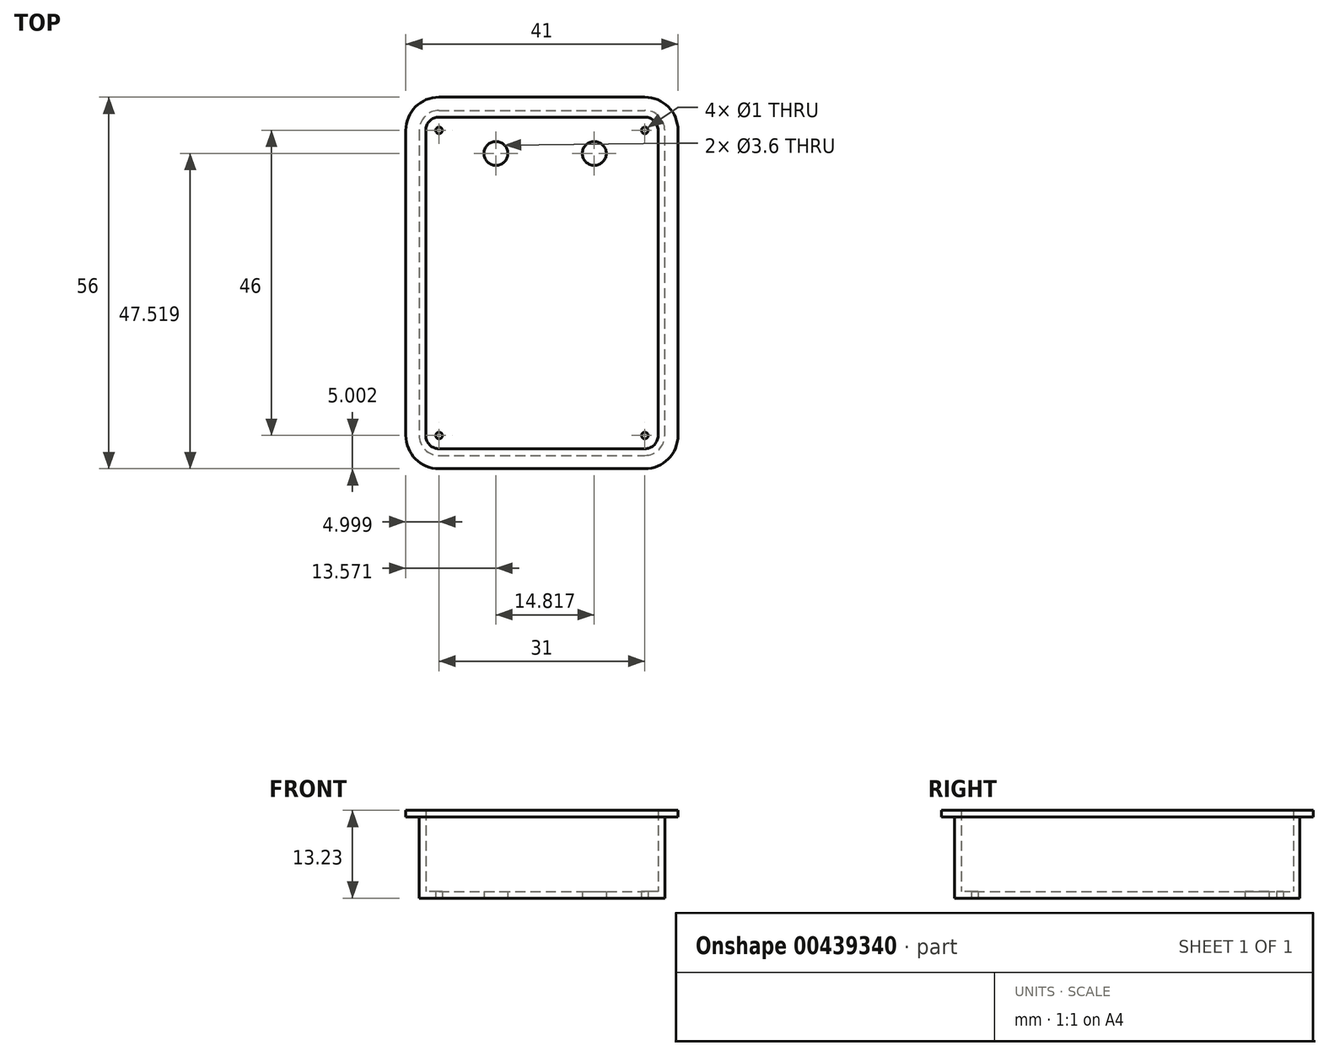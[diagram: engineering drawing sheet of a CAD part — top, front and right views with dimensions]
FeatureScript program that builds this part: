
annotation { "Feature Type Name" : "Feature", "Feature Type Description" : "" }
export const myFeature = defineFeature(function(context is Context, id is Id, definition is map)
    precondition{}
    {
        {
            var Q0;
            Q0=qCreatedBy(makeId("Top.planeOp"),FACE);
            var sketch = newSketch(context, id + "F0", { "sketchPlane" : qUnion([Q0])});
            skLineSegment(sketch, "E0.bottom", {"start": v(-15.84, -22.1) * mm, "end": v(15.16, -22.1) * mm});
            skLineSegment(sketch, "E0.top", {"start": v(-15.84, 27.9) * mm, "end": v(15.16, 27.9) * mm});
            skLineSegment(sketch, "E0.right", {"start": v(17.16, -20.1) * mm, "end": v(17.16, 25.9) * mm});
            skPoint(sketch, "E1.visualSharp", {"position": v(17.16, 27.9) * mm});
            skArc(sketch, "E1.filletArc", {"start": v(17.16, 25.9) * mm, "mid": v(16.57, 27.3) * mm, "end": v(15.16, 27.9) * mm});
            skPoint(sketch, "E2.visualSharp", {"position": v(17.16, -22.1) * mm});
            skArc(sketch, "E2.filletArc", {"start": v(15.16, -22.1) * mm, "mid": v(16.57, -21.52) * mm, "end": v(17.16, -20.1) * mm});
            skLineSegment(sketch, "E3", {"start": v(-17.84, 25.9) * mm, "end": v(-17.84, -20.1) * mm});
            skPoint(sketch, "E4.visualSharp", {"position": v(-17.84, 27.9) * mm});
            skArc(sketch, "E4.filletArc", {"start": v(-15.84, 27.9) * mm, "mid": v(-17.26, 27.3) * mm, "end": v(-17.84, 25.9) * mm});
            skPoint(sketch, "E5.visualSharp", {"position": v(-17.84, -22.1) * mm});
            skArc(sketch, "E5.filletArc", {"start": v(-17.84, -20.1) * mm, "mid": v(-17.26, -21.52) * mm, "end": v(-15.84, -22.1) * mm});
            skCircle(sketch, "E6", {"center": v(-15.84, -20.1) * mm, "radius": 0.5 * mm});
            skCircle(sketch, "E7", {"center": v(-15.84, 25.9) * mm, "radius": 0.5 * mm});
            skCircle(sketch, "E8", {"center": v(15.16, 25.9) * mm, "radius": 0.5 * mm});
            skCircle(sketch, "E9", {"center": v(15.16, -20.1) * mm, "radius": 0.5 * mm});
            skArc(sketch, "E10.0", {"start": v(-15.84, 28.9) * mm, "mid": v(-17.96, 28.01) * mm, "end": v(-18.84, 25.9) * mm});
            skLineSegment(sketch, "E10.1", {"start": v(-18.84, 25.9) * mm, "end": v(-18.84, -20.1) * mm});
            skLineSegment(sketch, "E10.2", {"start": v(-15.84, 28.9) * mm, "end": v(15.16, 28.9) * mm});
            skArc(sketch, "E10.3", {"start": v(-18.84, -20.1) * mm, "mid": v(-17.96, -22.23) * mm, "end": v(-15.84, -23.1) * mm});
            skArc(sketch, "E10.4", {"start": v(18.16, 25.9) * mm, "mid": v(17.28, 28.01) * mm, "end": v(15.16, 28.9) * mm});
            skLineSegment(sketch, "E10.5", {"start": v(18.16, -20.1) * mm, "end": v(18.16, 25.9) * mm});
            skArc(sketch, "E10.6", {"start": v(15.16, -23.1) * mm, "mid": v(17.28, -22.23) * mm, "end": v(18.16, -20.1) * mm});
            skLineSegment(sketch, "E10.7", {"start": v(-15.84, -23.1) * mm, "end": v(15.16, -23.1) * mm});
            skSolve(sketch);
        }
        {
            var Q0;
            Q0=makeQuery(id+"F0.imprint","IMPRINT",FACE,{"disambiguationData":[TD([[makeQuery(id+"F0.imprint","IMPRINT",EDGE,{"derivedFrom":sQuery(id+"F0.wireOp",EDGE,"E0.bottom")}),1.0]])]});
            extrude(context, id + "F1", {"entities" : qUnion([Q0]), "depth" : 1 * mm});
        }
        {
            var Q0;
            Q0=makeQuery(id+"F0.imprint","IMPRINT",FACE,{"disambiguationData":[TD([[makeQuery(id+"F0.imprint","IMPRINT",EDGE,{"derivedFrom":sQuery(id+"F0.wireOp",EDGE,"E0.bottom")}),-1.0]])]});
            extrude(context, id + "F2", {"entities" : qUnion([Q0]), "operationType" : NewBodyOperationType.ADD, "depth" : 13.23 * mm});
        }
        {
            var Q0;
            {var subQ0=sQuery(id+"F0.wireOp",EDGE,"E5.filletArc");var subQ1=sQuery(id+"F0.wireOp",EDGE,"E4.filletArc");var subQ2=sQuery(id+"F0.wireOp",EDGE,"E3");var subQ3=sQuery(id+"F0.wireOp",EDGE,"E2.filletArc");var subQ4=sQuery(id+"F0.wireOp",EDGE,"E1.filletArc");var subQ5=sQuery(id+"F0.wireOp",EDGE,"E0.right");var subQ6=sQuery(id+"F0.wireOp",EDGE,"E0.top");var subQ7=sQuery(id+"F0.wireOp",EDGE,"E0.bottom");Q0=makeQuery(id+"F2.boolean.opBoolean","MERGE",FACE,{"derivedFrom":[makeQuery(id+"F1.opExtrude","CAP_FACE",FACE,{"disambiguationData":[OSD([subQ7,subQ6,subQ5,subQ4,subQ3,subQ2,subQ1,subQ0,sQuery(id+"F0.wireOp",EDGE,"E6"),sQuery(id+"F0.wireOp",EDGE,"E7"),sQuery(id+"F0.wireOp",EDGE,"E8"),sQuery(id+"F0.wireOp",EDGE,"E9")])],"isStart":true}),makeQuery(id+"F2.opExtrude","CAP_FACE",FACE,{"disambiguationData":[OSD([subQ7,subQ6,subQ5,subQ4,subQ3,subQ2,subQ1,subQ0,sQuery(id+"F0.wireOp",EDGE,"E10.0"),sQuery(id+"F0.wireOp",EDGE,"E10.1"),sQuery(id+"F0.wireOp",EDGE,"E10.2"),sQuery(id+"F0.wireOp",EDGE,"E10.3"),sQuery(id+"F0.wireOp",EDGE,"E10.4"),sQuery(id+"F0.wireOp",EDGE,"E10.5"),sQuery(id+"F0.wireOp",EDGE,"E10.6"),sQuery(id+"F0.wireOp",EDGE,"E10.7")])],"isStart":true})]});}
            var sketch = newSketch(context, id + "F3", { "sketchPlane" : qUnion([Q0])});
            skCircle(sketch, "E11", {"center": v(7.55, -22.4) * mm, "radius": 1.8 * mm});
            skCircle(sketch, "E12", {"center": v(-7.27, -22.4) * mm, "radius": 1.8 * mm});
            skSolve(sketch);
        }
        {
            var Q0;
            Q0=makeQuery(id+"F3.imprint","IMPRINT",FACE,{"disambiguationData":[TD([[makeQuery(id+"F3.imprint","IMPRINT",EDGE,{"derivedFrom":sQuery(id+"F3.wireOp",EDGE,"E12")}),1.0]])]});
            var Q1;
            Q1=makeQuery(id+"F3.imprint","IMPRINT",FACE,{"disambiguationData":[TD([[makeQuery(id+"F3.imprint","IMPRINT",EDGE,{"derivedFrom":sQuery(id+"F3.wireOp",EDGE,"E11")}),1.0]])]});
            extrude(context, id + "F4", {"entities" : qUnion([Q0, Q1]), "operationType" : NewBodyOperationType.REMOVE, "oppositeDirection" : true, "depth" : 1 * mm});
        }
        {
            var Q0;
            Q0=makeQuery(id+"F2.opExtrude","CAP_FACE",FACE,{"disambiguationData":[OSD([sQuery(id+"F0.wireOp",EDGE,"E0.bottom"),sQuery(id+"F0.wireOp",EDGE,"E0.top"),sQuery(id+"F0.wireOp",EDGE,"E0.right"),sQuery(id+"F0.wireOp",EDGE,"E1.filletArc"),sQuery(id+"F0.wireOp",EDGE,"E2.filletArc"),sQuery(id+"F0.wireOp",EDGE,"E3"),sQuery(id+"F0.wireOp",EDGE,"E4.filletArc"),sQuery(id+"F0.wireOp",EDGE,"E5.filletArc"),sQuery(id+"F0.wireOp",EDGE,"E10.0"),sQuery(id+"F0.wireOp",EDGE,"E10.1"),sQuery(id+"F0.wireOp",EDGE,"E10.2"),sQuery(id+"F0.wireOp",EDGE,"E10.3"),sQuery(id+"F0.wireOp",EDGE,"E10.4"),sQuery(id+"F0.wireOp",EDGE,"E10.5"),sQuery(id+"F0.wireOp",EDGE,"E10.6"),sQuery(id+"F0.wireOp",EDGE,"E10.7")])],"isStart":false});
            var sketch = newSketch(context, id + "F5", { "sketchPlane" : qUnion([Q0])});
            skArc(sketch, "E13.0", {"start": v(-15.84, 30.9) * mm, "mid": v(-19.38, 29.43) * mm, "end": v(-20.84, 25.9) * mm});
            skLineSegment(sketch, "E13.1", {"start": v(-20.84, 25.9) * mm, "end": v(-20.84, -20.1) * mm});
            skLineSegment(sketch, "E13.2", {"start": v(-15.84, 30.9) * mm, "end": v(15.16, 30.9) * mm});
            skArc(sketch, "E13.3", {"start": v(-20.84, -20.1) * mm, "mid": v(-19.38, -23.64) * mm, "end": v(-15.84, -25.1) * mm});
            skArc(sketch, "E13.4", {"start": v(20.16, 25.9) * mm, "mid": v(18.7, 29.43) * mm, "end": v(15.16, 30.9) * mm});
            skLineSegment(sketch, "E13.5", {"start": v(20.16, -20.1) * mm, "end": v(20.16, 25.9) * mm});
            skArc(sketch, "E13.6", {"start": v(15.16, -25.1) * mm, "mid": v(18.7, -23.64) * mm, "end": v(20.16, -20.1) * mm});
            skLineSegment(sketch, "E13.7", {"start": v(-15.84, -25.1) * mm, "end": v(15.16, -25.1) * mm});
            skSolve(sketch);
        }
        {
            var Q0;
            Q0=makeQuery(id+"F5.imprint","IMPRINT",FACE,{"disambiguationData":[TD([[makeQuery(id+"F5.imprint","IMPRINT",EDGE,{"derivedFrom":sQuery(id+"F5.wireOp",EDGE,"E13.0")}),1.0]])]});
            extrude(context, id + "F6", {"entities" : qUnion([Q0]), "operationType" : NewBodyOperationType.ADD, "oppositeDirection" : true, "depth" : 1 * mm});
        }
    });
